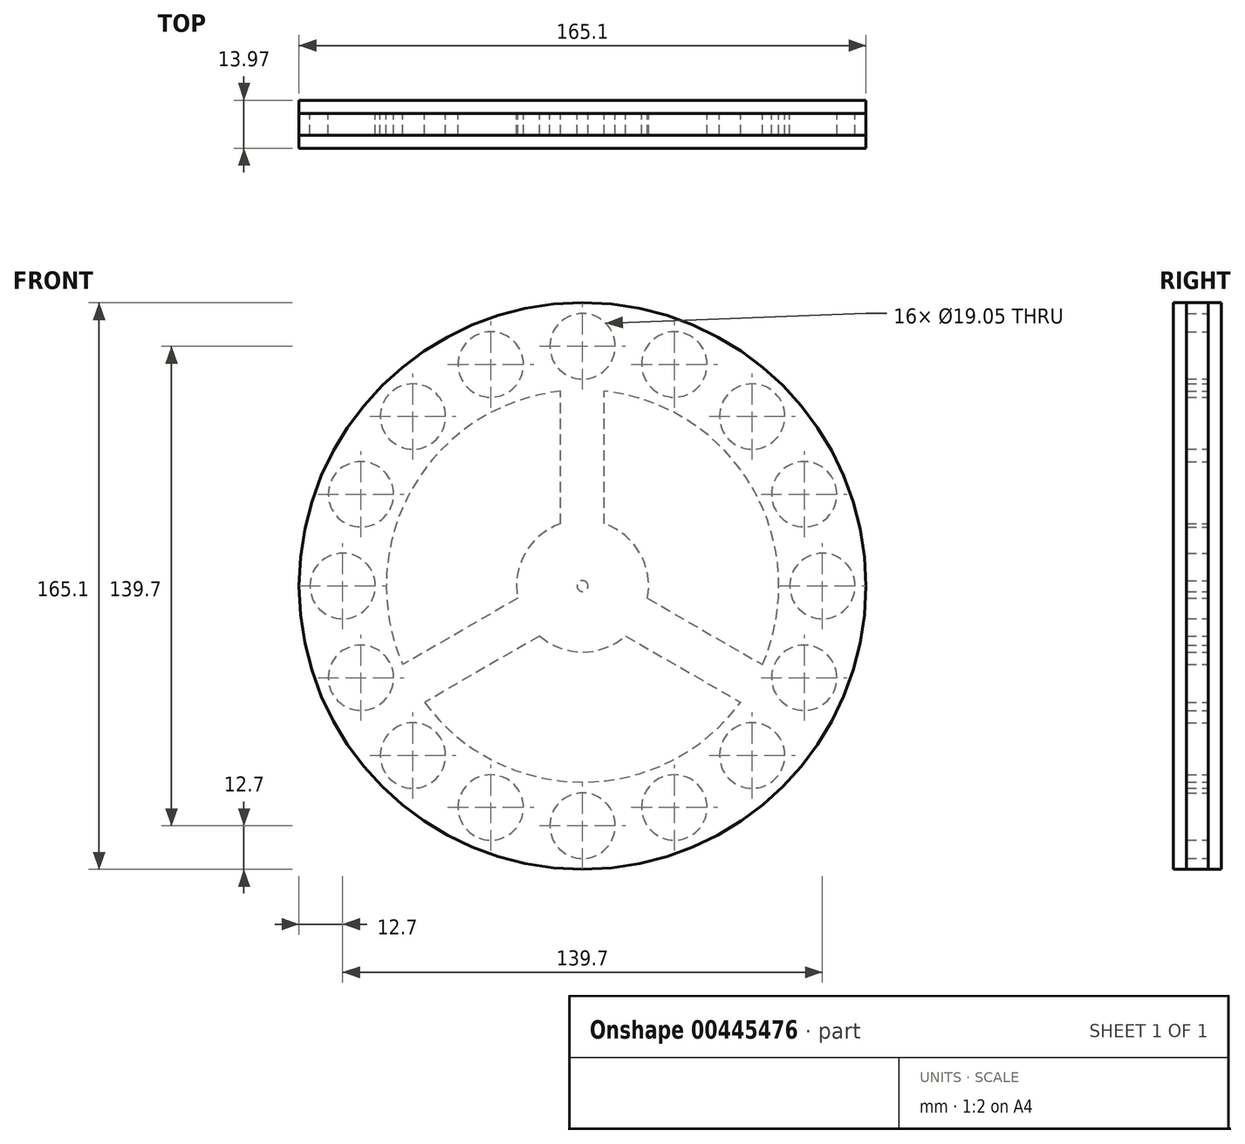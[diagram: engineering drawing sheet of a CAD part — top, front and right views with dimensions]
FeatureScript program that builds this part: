
annotation { "Feature Type Name" : "Feature", "Feature Type Description" : "" }
export const myFeature = defineFeature(function(context is Context, id is Id, definition is map)
    precondition{}
    {
        {
            var Q0;
            Q0=qCreatedBy(makeId("Front.planeOp"),FACE);
            var sketch = newSketch(context, id + "F0", { "sketchPlane" : qUnion([Q0])});
            skCircle(sketch, "E0", {"center": v(0, 0) * mm, "radius": 82.55 * mm});
            skCircle(sketch, "E1", {"center": v(0, 0) * mm, "radius": 57.15 * mm});
            skCircle(sketch, "E2", {"center": v(0, 69.85) * mm, "radius": 9.53 * mm});
            skCircle(sketch, "E3.1.0", {"center": v(-26.73, 64.53) * mm, "radius": 9.53 * mm});
            skCircle(sketch, "E3.2.0", {"center": v(-49.4, 49.4) * mm, "radius": 9.53 * mm});
            skCircle(sketch, "E3.3.0", {"center": v(-64.53, 26.73) * mm, "radius": 9.53 * mm});
            skCircle(sketch, "E3.4.0", {"center": v(-69.85, 0) * mm, "radius": 9.53 * mm});
            skCircle(sketch, "E3.5.0", {"center": v(-64.53, -26.73) * mm, "radius": 9.53 * mm});
            skCircle(sketch, "E3.6.0", {"center": v(-49.4, -49.4) * mm, "radius": 9.53 * mm});
            skCircle(sketch, "E3.7.0", {"center": v(-26.73, -64.53) * mm, "radius": 9.53 * mm});
            skCircle(sketch, "E3.8.0", {"center": v(0, -69.85) * mm, "radius": 9.53 * mm});
            skCircle(sketch, "E3.9.0", {"center": v(26.73, -64.53) * mm, "radius": 9.53 * mm});
            skCircle(sketch, "E3.10.0", {"center": v(49.4, -49.4) * mm, "radius": 9.53 * mm});
            skCircle(sketch, "E3.11.0", {"center": v(64.53, -26.73) * mm, "radius": 9.53 * mm});
            skCircle(sketch, "E3.12.0", {"center": v(69.85, 0) * mm, "radius": 9.53 * mm});
            skCircle(sketch, "E3.13.0", {"center": v(64.53, 26.73) * mm, "radius": 9.53 * mm});
            skCircle(sketch, "E3.14.0", {"center": v(49.4, 49.4) * mm, "radius": 9.53 * mm});
            skCircle(sketch, "E3.15.0", {"center": v(26.73, 64.53) * mm, "radius": 9.53 * mm});
            skCircle(sketch, "E4", {"center": v(0, 0) * mm, "radius": 19.24 * mm});
            skLineSegment(sketch, "E5", {"start": v(0, 0) * mm, "end": v(0, 69.85) * mm, "construction": true});
            skLineSegment(sketch, "E6.0", {"start": v(6.35, 18.16) * mm, "end": v(6.35, 56.8) * mm});
            skLineSegment(sketch, "E7.0", {"start": v(-6.35, 18.16) * mm, "end": v(-6.35, 56.8) * mm});
            skLineSegment(sketch, "E8.1.0", {"start": v(-12.55, -14.58) * mm, "end": v(-46.01, -33.9) * mm});
            skLineSegment(sketch, "E8.1.1", {"start": v(-18.9, -3.58) * mm, "end": v(-52.36, -22.9) * mm});
            skLineSegment(sketch, "E8.2.0", {"start": v(18.9, -3.58) * mm, "end": v(52.36, -22.9) * mm});
            skLineSegment(sketch, "E8.2.1", {"start": v(12.55, -14.58) * mm, "end": v(46.01, -33.9) * mm});
            skCircle(sketch, "E9", {"center": v(0, 0) * mm, "radius": 1.59 * mm});
            skSolve(sketch);
        }
        {
            var Q0;
            Q0 = qSketchRegion(id + "F0", true);
            var Q1;
            {var subQ0=sQuery(id+"F0.wireOp",EDGE,"E6.0");var subQ1=sQuery(id+"F0.wireOp",EDGE,"E1");var subQ2=makeQuery(id+"F0.imprint","INTERSECT",VERTEX,{"derivedFrom":[subQ1,subQ0]});Q1=makeQuery(id+"F0.imprint","IMPRINT",FACE,{"disambiguationData":[TD([[makeQuery(id+"F0.imprint","IMPRINT",EDGE,{"disambiguationData":[TD([[subQ2,-1.0]])],"derivedFrom":subQ1}),1.0]])]});}
            var Q2;
            {var subQ0=sQuery(id+"F0.wireOp",EDGE,"E6.0");var subQ1=sQuery(id+"F0.wireOp",EDGE,"E1");var subQ2=makeQuery(id+"F0.imprint","INTERSECT",VERTEX,{"derivedFrom":[subQ1,subQ0]});Q2=makeQuery(id+"F0.imprint","IMPRINT",FACE,{"disambiguationData":[TD([[makeQuery(id+"F0.imprint","IMPRINT",EDGE,{"disambiguationData":[TD([[subQ2,-1.0]])],"derivedFrom":subQ1}),-1.0]])]});}
            var Q3;
            {var subQ0=sQuery(id+"F0.wireOp",EDGE,"E4");var subQ1=makeQuery(id+"F0.imprint","INTERSECT",VERTEX,{"derivedFrom":[subQ0,sQuery(id+"F0.wireOp",EDGE,"E6.0")]});Q3=makeQuery(id+"F0.imprint","IMPRINT",FACE,{"disambiguationData":[TD([[makeQuery(id+"F0.imprint","IMPRINT",EDGE,{"disambiguationData":[TD([[subQ1,-1.0]])],"derivedFrom":subQ0}),1.0]])]});}
            var Q4;
            {var subQ0=sQuery(id+"F0.wireOp",EDGE,"E8.1.0");Q4=makeQuery(id+"F0.imprint","IMPRINT",FACE,{"disambiguationData":[TD([[makeQuery(id+"F0.imprint","IMPRINT",EDGE,{"derivedFrom":subQ0}),-1.0]])]});}
            var Q5;
            {var subQ0=sQuery(id+"F0.wireOp",EDGE,"E8.2.0");Q5=makeQuery(id+"F0.imprint","IMPRINT",FACE,{"disambiguationData":[TD([[makeQuery(id+"F0.imprint","IMPRINT",EDGE,{"derivedFrom":subQ0}),-1.0]])]});}
            extrude(context, id + "F1", {"entities" : qUnion([Q0, Q1, Q2, Q3, Q4, Q5]), "depth" : 6.35 * mm});
        }
        {
            var Q0;
            Q0=makeQuery(id+"F1.opExtrude","CAP_FACE",FACE,{"disambiguationData":[OSD([sQuery(id+"F0.wireOp",EDGE,"E0"),sQuery(id+"F0.wireOp",EDGE,"E1"),sQuery(id+"F0.wireOp",EDGE,"E2"),sQuery(id+"F0.wireOp",EDGE,"E3.1.0"),sQuery(id+"F0.wireOp",EDGE,"E3.2.0"),sQuery(id+"F0.wireOp",EDGE,"E3.3.0"),sQuery(id+"F0.wireOp",EDGE,"E3.4.0"),sQuery(id+"F0.wireOp",EDGE,"E3.5.0"),sQuery(id+"F0.wireOp",EDGE,"E3.6.0"),sQuery(id+"F0.wireOp",EDGE,"E3.7.0"),sQuery(id+"F0.wireOp",EDGE,"E3.8.0"),sQuery(id+"F0.wireOp",EDGE,"E3.9.0"),sQuery(id+"F0.wireOp",EDGE,"E3.10.0"),sQuery(id+"F0.wireOp",EDGE,"E3.11.0"),sQuery(id+"F0.wireOp",EDGE,"E3.12.0"),sQuery(id+"F0.wireOp",EDGE,"E3.13.0"),sQuery(id+"F0.wireOp",EDGE,"E3.14.0"),sQuery(id+"F0.wireOp",EDGE,"E3.15.0")])],"isStart":false});
            var sketch = newSketch(context, id + "F2", { "sketchPlane" : qUnion([Q0])});
            skCircle(sketch, "E10", {"center": v(0, 0) * mm, "radius": 1.59 * mm});
            skSolve(sketch);
        }
        {
            var Q0;
            Q0=makeQuery(id+"F2.imprint","IMPRINT",FACE,{"disambiguationData":[TD([[makeQuery(id+"F2.imprint","IMPRINT",EDGE,{"derivedFrom":sQuery(id+"F2.wireOp",EDGE,"E10")}),1.0]])]});
            extrude(context, id + "F3", {"entities" : qUnion([Q0]), "operationType" : NewBodyOperationType.REMOVE, "oppositeDirection" : true, "depth" : 25.4 * mm});
        }
        {
            var Q0;
            Q0=makeQuery(id+"F1.opExtrude","CAP_FACE",FACE,{"disambiguationData":[OSD([sQuery(id+"F0.wireOp",EDGE,"E0"),sQuery(id+"F0.wireOp",EDGE,"E1"),sQuery(id+"F0.wireOp",EDGE,"E2"),sQuery(id+"F0.wireOp",EDGE,"E3.1.0"),sQuery(id+"F0.wireOp",EDGE,"E3.2.0"),sQuery(id+"F0.wireOp",EDGE,"E3.3.0"),sQuery(id+"F0.wireOp",EDGE,"E3.4.0"),sQuery(id+"F0.wireOp",EDGE,"E3.5.0"),sQuery(id+"F0.wireOp",EDGE,"E3.6.0"),sQuery(id+"F0.wireOp",EDGE,"E3.7.0"),sQuery(id+"F0.wireOp",EDGE,"E3.8.0"),sQuery(id+"F0.wireOp",EDGE,"E3.9.0"),sQuery(id+"F0.wireOp",EDGE,"E3.10.0"),sQuery(id+"F0.wireOp",EDGE,"E3.11.0"),sQuery(id+"F0.wireOp",EDGE,"E3.12.0"),sQuery(id+"F0.wireOp",EDGE,"E3.13.0"),sQuery(id+"F0.wireOp",EDGE,"E3.14.0"),sQuery(id+"F0.wireOp",EDGE,"E3.15.0"),sQuery(id+"F0.wireOp",EDGE,"E4"),sQuery(id+"F0.wireOp",EDGE,"E6.0"),sQuery(id+"F0.wireOp",EDGE,"E7.0"),sQuery(id+"F0.wireOp",EDGE,"E8.1.0"),sQuery(id+"F0.wireOp",EDGE,"E8.1.1"),sQuery(id+"F0.wireOp",EDGE,"E8.2.0"),sQuery(id+"F0.wireOp",EDGE,"E8.2.1"),sQuery(id+"F0.wireOp",EDGE,"E9")])],"isStart":false});
            var sketch = newSketch(context, id + "F4", { "sketchPlane" : qUnion([Q0])});
            skCircle(sketch, "E11.0", {"center": v(0, 0) * mm, "radius": 82.55 * mm});
            skSolve(sketch);
        }
        {
            var Q0;
            Q0 = qSketchRegion(id + "F4", true);
            extrude(context, id + "F5", {"entities" : qUnion([Q0]), "depth" : 3.8 * mm});
        }
        {
            var Q0;
            Q0=makeQuery(id+"F1.opExtrude","CAP_FACE",FACE,{"disambiguationData":[OSD([sQuery(id+"F0.wireOp",EDGE,"E0"),sQuery(id+"F0.wireOp",EDGE,"E1"),sQuery(id+"F0.wireOp",EDGE,"E2"),sQuery(id+"F0.wireOp",EDGE,"E3.1.0"),sQuery(id+"F0.wireOp",EDGE,"E3.2.0"),sQuery(id+"F0.wireOp",EDGE,"E3.3.0"),sQuery(id+"F0.wireOp",EDGE,"E3.4.0"),sQuery(id+"F0.wireOp",EDGE,"E3.5.0"),sQuery(id+"F0.wireOp",EDGE,"E3.6.0"),sQuery(id+"F0.wireOp",EDGE,"E3.7.0"),sQuery(id+"F0.wireOp",EDGE,"E3.8.0"),sQuery(id+"F0.wireOp",EDGE,"E3.9.0"),sQuery(id+"F0.wireOp",EDGE,"E3.10.0"),sQuery(id+"F0.wireOp",EDGE,"E3.11.0"),sQuery(id+"F0.wireOp",EDGE,"E3.12.0"),sQuery(id+"F0.wireOp",EDGE,"E3.13.0"),sQuery(id+"F0.wireOp",EDGE,"E3.14.0"),sQuery(id+"F0.wireOp",EDGE,"E3.15.0"),sQuery(id+"F0.wireOp",EDGE,"E4"),sQuery(id+"F0.wireOp",EDGE,"E6.0"),sQuery(id+"F0.wireOp",EDGE,"E7.0"),sQuery(id+"F0.wireOp",EDGE,"E8.1.0"),sQuery(id+"F0.wireOp",EDGE,"E8.1.1"),sQuery(id+"F0.wireOp",EDGE,"E8.2.0"),sQuery(id+"F0.wireOp",EDGE,"E8.2.1"),sQuery(id+"F0.wireOp",EDGE,"E9")])],"isStart":true});
            var sketch = newSketch(context, id + "F6", { "sketchPlane" : qUnion([Q0])});
            skCircle(sketch, "E12", {"center": v(0, 0) * mm, "radius": 82.55 * mm});
            skSolve(sketch);
        }
        {
            var Q0;
            Q0 = qSketchRegion(id + "F6", true);
            extrude(context, id + "F7", {"entities" : qUnion([Q0]), "depth" : 3.8 * mm});
        }
    });
